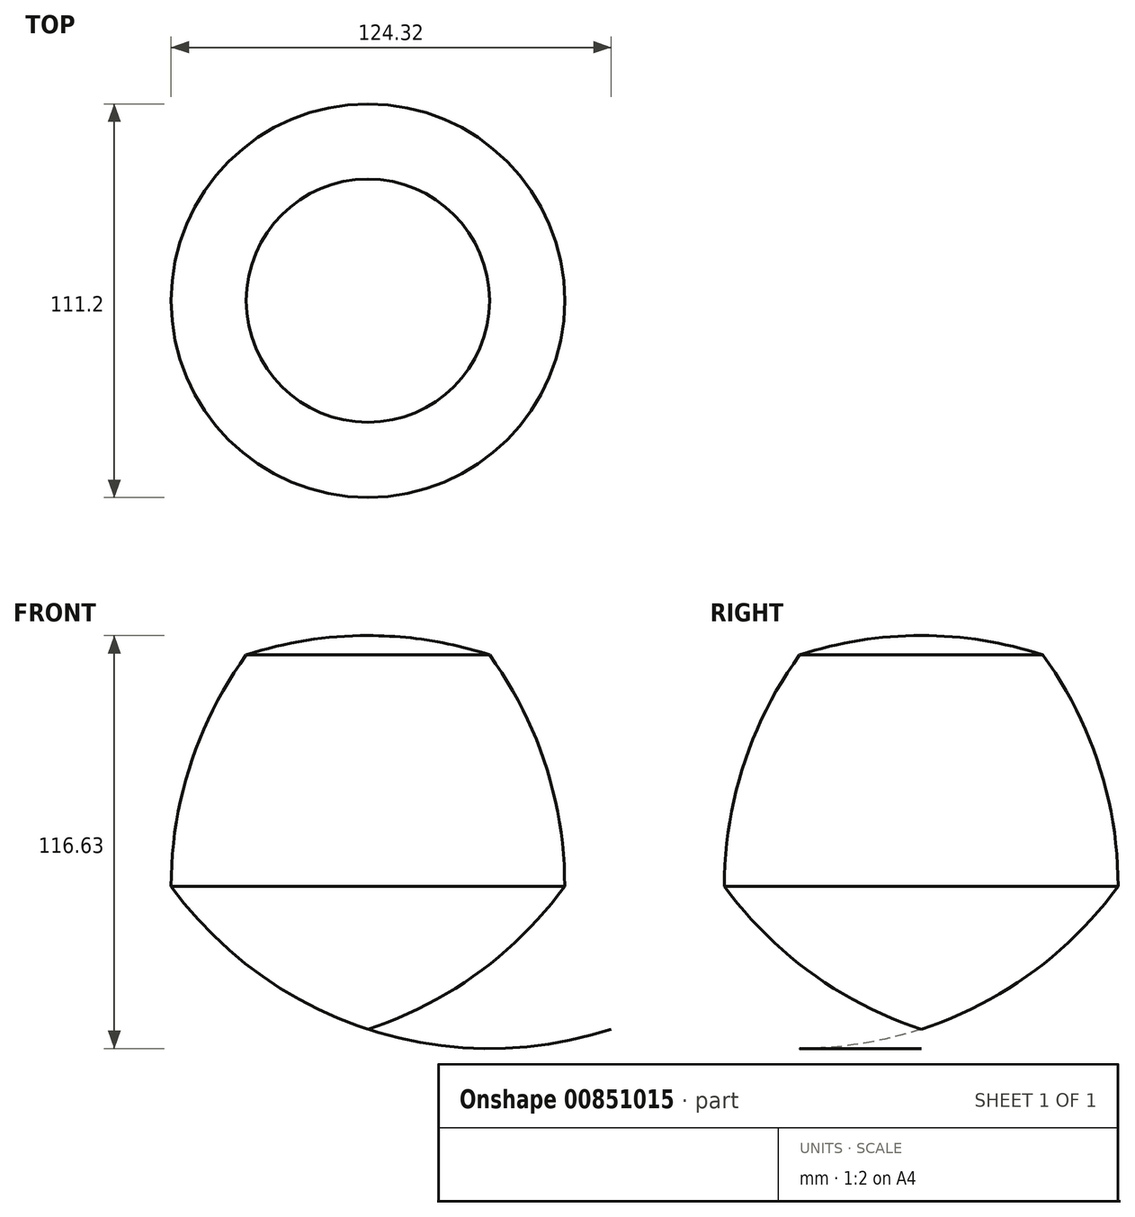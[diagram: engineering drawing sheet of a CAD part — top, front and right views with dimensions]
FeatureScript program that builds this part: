
annotation { "Feature Type Name" : "Feature", "Feature Type Description" : "" }
export const myFeature = defineFeature(function(context is Context, id is Id, definition is map)
    precondition{}
    {
        {
            var Q0;
            Q0=qCreatedBy(makeId("Front.planeOp"),FACE);
            var sketch = newSketch(context, id + "F0", { "sketchPlane" : qUnion([Q0])});
            skCircle(sketch, "E0.cCircle", {"center": v(0, 0) * mm, "radius": 47.3 * mm, "construction": true});
            skLineSegment(sketch, "E0.0", {"start": v(-34.36, 47.3) * mm, "end": v(34.36, 47.3) * mm, "construction": true});
            skLineSegment(sketch, "E0.1", {"start": v(34.36, 47.3) * mm, "end": v(55.6, -18.06) * mm, "construction": true});
            skLineSegment(sketch, "E0.2", {"start": v(55.6, -18.06) * mm, "end": v(0, -58.46) * mm, "construction": true});
            skLineSegment(sketch, "E0.3", {"start": v(0, -58.46) * mm, "end": v(-55.6, -18.06) * mm, "construction": true});
            skLineSegment(sketch, "E0.4", {"start": v(-55.6, -18.06) * mm, "end": v(-34.36, 47.3) * mm, "construction": true});
            skPoint(sketch, "E0.0.midPoint", {"position": v(0, 47.3) * mm});
            skArc(sketch, "E1", {"start": v(-55.6, -18.06) * mm, "mid": v(-31, -42.66) * mm, "end": v(0, -58.46) * mm});
            skArc(sketch, "E2", {"start": v(-34.36, 47.3) * mm, "mid": v(-50.15, 16.3) * mm, "end": v(-55.6, -18.06) * mm});
            skPoint(sketch, "E3", {"position": v(0, 52.73) * mm});
            skLineSegment(sketch, "E4", {"start": v(0, 52.73) * mm, "end": v(0, -58.46) * mm});
            skArc(sketch, "E5", {"start": v(0, 52.73) * mm, "mid": v(-17.4, 51.37) * mm, "end": v(-34.36, 47.3) * mm});
            skSolve(sketch);
        }
        {
            var Q0;
            Q0=makeQuery(id+"F0.imprint","IMPRINT",FACE,{"disambiguationData":[TD([[makeQuery(id+"F0.imprint","IMPRINT",EDGE,{"derivedFrom":sQuery(id+"F0.wireOp",EDGE,"E1")}),1.0]])]});
            var Q1;
            Q1=sQuery(id+"F0.wireOp",EDGE,"E4");
            revolve(context, id + "F1", {"surfaceOperationType" : NewSurfaceOperationType.NEW, "entities" : qUnion([Q0]), "axis" : qUnion([Q1]), "revolveType" : RevolveType.FULL});
        }
    });
